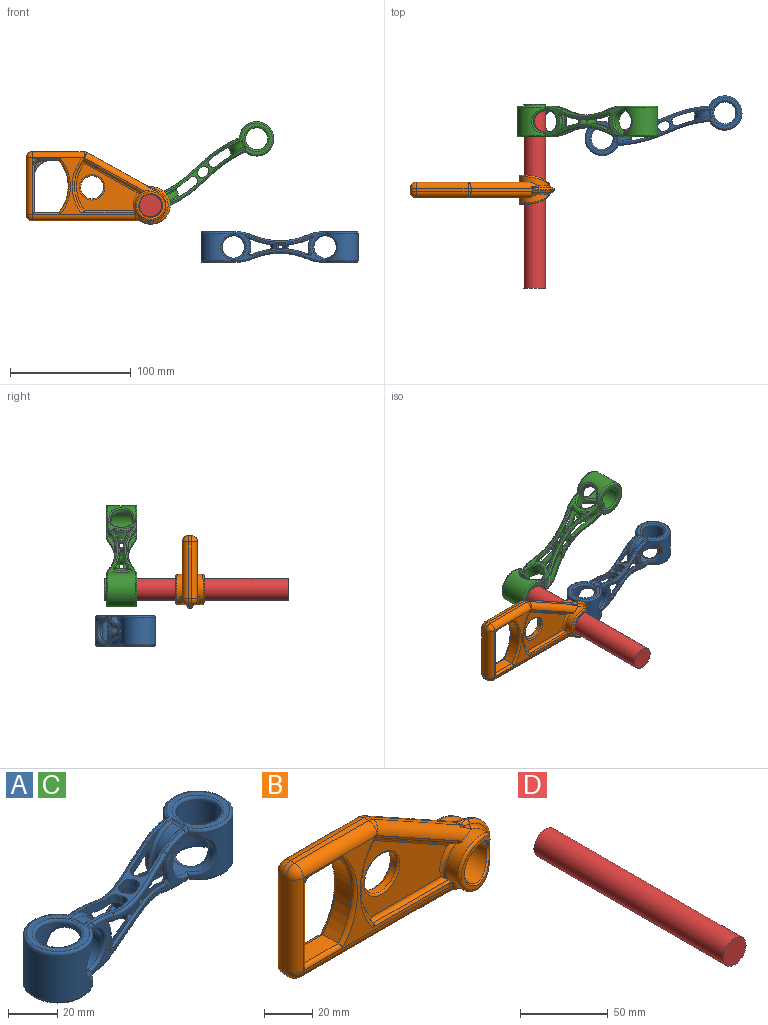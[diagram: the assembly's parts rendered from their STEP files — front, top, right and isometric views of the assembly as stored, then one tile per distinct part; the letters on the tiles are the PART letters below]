
ASSEMBLY  parts=4 mates=2
PART A: 148 faces, bbox 132.7x52.1x26.6 mm
  f0: extruded ~21.29x15.47mm, area 60mm2, adj f2,f5,f6,f9,f89,f90,f106,f124
  f1: extruded ~30.64x19.59mm, area 94.2mm2, adj f2,f3,f4,f11,f13,f15,f17,f19
  f2: bspline ~51.5x17.79mm, area 103.2mm2, adj f0,f1,f8,f109,f111,f130,f131,f132
  f3: extruded ~25.18x24.71mm, area 181.7mm2, adj f1,f34,f55,f56,f59,f64,f94,f95
  f4: extruded ~25.24x22.45mm, area 174.2mm2, adj f1,f35,f55,f56,f60,f63,f96,f98
  f5: extruded ~25.36x23.65mm, area 171.9mm2, adj f0,f38,f55,f56,f58,f61,f89,f91
  f6: extruded ~25.85x25.34mm, area 182.8mm2, adj f0,f39,f55,f56,f57,f62,f90,f92
  f7: extruded ~76.15x22.86mm, area 322.9mm2, adj f26,f27,f45,f47,f65,f67,f69,f71
  f8: extruded ~76.19x22.86mm, area 349.2mm2, adj f2,f26,f27,f43,f48,f68,f70,f72
  f9: cylinder r=7.62mm len=3.81mm, axis (0,0,-1), area 1.8mm2, adj f0,f56,f124,f126
  f10: cylinder r=7.62mm len=3.81mm, axis (0,0,-1), area 1.8mm2, adj f55,f99,f112,f113
  f11: cylinder r=7.62mm len=3.91mm, axis (0,0,-1), area 1.9mm2, adj f1,f56,f114,f115
  f12: cylinder r=7.62mm len=3.91mm, axis (0,0,-1), area 1.9mm2, adj f55,f99,f121,f123
  f13: cylinder r=5.08mm len=3.89mm, axis (0,0,-1), area 8.8mm2, adj f1,f56,f120,f122
  f14: cylinder r=5.08mm len=3.89mm, axis (0,0,-1), area 8.8mm2, adj f55,f99,f116,f118
  f15: cylinder r=5.08mm len=3.88mm, axis (0,0,-1), area 8.6mm2, adj f1,f56,f125,f127
  f16: cylinder r=5.08mm len=3.88mm, axis (0,0,-1), area 8.6mm2, adj f55,f99,f117,f119
  f17: extruded ~3.88x2.73mm, area 11.3mm2, adj f1,f56,f122,f125
  f18: extruded ~3.88x2.73mm, area 11.3mm2, adj f55,f99,f116,f117
  f19: extruded ~3.88x2.98mm, area 12.2mm2, adj f1,f56,f120,f127
  f20: extruded ~3.88x2.98mm, area 12.2mm2, adj f55,f99,f118,f119
  f21: plane 27.31x26.12mm, normal (0,0,1), area 177.8mm2, adj f33,f34,f35,f53,f59,f60,f85,f87
  f22: plane 27.87x26.19mm, normal (0,0,1), area 179.1mm2, adj f38,f39,f40,f54,f57,f58,f77,f78
  f23: plane 27.31x26.12mm, normal (0,0,-1), area 177.8mm2, adj f34,f35,f36,f51,f63,f64,f73,f75
  f24: plane 27.87x26.19mm, normal (0,0,-1), area 179.1mm2, adj f37,f38,f39,f52,f61,f62,f65,f66
  f25: cylinder r=9.14mm len=22.73mm, axis (0,0,-1), area 886.6mm2, adj f41,f51,f53
  f26: cylinder r=14.22mm len=28.45mm, axis (0,0,-1), area 1302.5mm2, adj f7,f8,f42,f43,f44,f45,f75,f87
  f27: cylinder r=14.22mm len=28.45mm, axis (0,0,-1), area 1277mm2, adj f7,f8,f46,f47,f48,f49,f66,f78
  f28: cylinder r=9.14mm len=22.73mm, axis (0,0,-1), area 864.6mm2, adj f50,f52,f54
  f29: cylinder r=9.27mm len=25.51mm, axis (0,1,0), area 486.9mm2, adj f46,f47,f48,f49,f50
  f30: cylinder r=9.27mm len=25.34mm, axis (0,1,0), area 493.1mm2, adj f41,f42,f43,f44,f45
  f31: cylinder r=11.81mm len=23.62mm, axis (0,1,0), area 180.4mm2, adj f37,f38,f39,f40
  f32: cylinder r=11.81mm len=23.62mm, axis (0,1,0), area 184.8mm2, adj f33,f34,f35,f36
  f33: bspline ~8.37x2.03mm, area 10.5mm2, adj f21,f32,f34,f35
  f34: bspline ~26.3x16.67mm, area 89mm2, adj f3,f21,f23,f32,f33,f36,f59,f64
  f35: bspline ~26.3x16.17mm, area 77.2mm2, adj f4,f21,f23,f32,f33,f36,f60,f63
  f36: bspline ~8.37x2.03mm, area 10.5mm2, adj f23,f32,f34,f35
  f37: bspline ~8.33x1.96mm, area 10.2mm2, adj f24,f31,f38,f39
  f38: bspline ~26.3x15.72mm, area 76.6mm2, adj f5,f22,f24,f31,f37,f40,f58,f61
  f39: bspline ~26.3x16.12mm, area 86.8mm2, adj f6,f22,f24,f31,f37,f40,f57,f62
  f40: bspline ~8.33x1.96mm, area 10.2mm2, adj f22,f31,f38,f39
  f41: bspline ~20.62x20.42mm, area 176.2mm2, adj f25,f30
  f42: bspline ~21.13x10.93mm, area 61mm2, adj f26,f30,f43
  f43: bspline ~21.24x13.49mm, area 62.6mm2, adj f8,f26,f30,f42
  f44: bspline ~21.18x11.16mm, area 65.1mm2, adj f26,f30,f45
  f45: bspline ~21.22x12.66mm, area 70.2mm2, adj f7,f26,f30,f44
  f46: bspline ~21.2x11.48mm, area 64.5mm2, adj f27,f29,f47
  f47: bspline ~21.22x12.32mm, area 61.2mm2, adj f7,f27,f29,f46
  f48: bspline ~21.23x13.02mm, area 67.6mm2, adj f8,f27,f29,f49
  f49: bspline ~21.21x11.56mm, area 68.4mm2, adj f27,f29,f48
  f50: bspline ~20.83x20.62mm, area 177.5mm2, adj f28,f29
  f51: torus R=10.48mm, axis (0,0,1), area 126.8mm2, adj f23,f25
  f52: torus R=10.48mm, axis (0,0,1), area 126.8mm2, adj f24,f28
  f53: torus R=10.48mm, axis (0,0,1), area 126.8mm2, adj f21,f25
  f54: torus R=10.48mm, axis (0,0,1), area 126.8mm2, adj f22,f28
  f55: cylinder r=57.15mm len=45.21mm, axis (0,1,0), area 182.1mm2, adj f3,f4,f5,f6,f10,f12,f14,f16
  f56: cylinder r=57.15mm len=45.21mm, axis (0,1,0), area 182.1mm2, adj f3,f4,f5,f6,f9,f11,f13,f15
  f57: cylinder r=34.92mm len=13.81mm, axis (0,1,0), area 18.5mm2, adj f6,f22,f39,f56,f82
  f58: cylinder r=34.92mm len=13.81mm, axis (0,1,0), area 17.9mm2, adj f5,f22,f38,f56,f79
  f59: cylinder r=34.92mm len=13.81mm, axis (0,1,0), area 18.2mm2, adj f3,f21,f34,f56,f83
  f60: cylinder r=34.92mm len=13.81mm, axis (0,1,0), area 18.5mm2, adj f4,f21,f35,f56,f86
  f61: cylinder r=34.92mm len=13.81mm, axis (0,1,0), area 17.9mm2, adj f5,f24,f38,f55,f67
  f62: cylinder r=34.92mm len=13.81mm, axis (0,1,0), area 18.5mm2, adj f6,f24,f39,f55,f70
  f63: cylinder r=34.92mm len=13.81mm, axis (0,1,0), area 18.5mm2, adj f4,f23,f35,f55,f74
  f64: cylinder r=34.92mm len=13.81mm, axis (0,1,0), area 18.2mm2, adj f3,f23,f34,f55,f71
  f65: bspline ~12.89x2.51mm, area 4.9mm2, adj f7,f24,f66,f67
  f66: torus R=12.95mm, axis (0,0,1), area 148.7mm2, adj f24,f27,f65,f68
  f67: bspline ~21.36x5.74mm, area 28.7mm2, adj f7,f61,f65,f69
  f68: bspline ~14.57x2.58mm, area 4.4mm2, adj f8,f24,f66,f70
  f69: bspline ~57.28x19.04mm, area 98.7mm2, adj f7,f55,f67,f71
  f70: bspline ~21.47x5.74mm, area 27.8mm2, adj f8,f62,f68,f72
  f71: bspline ~21.5x5.74mm, area 27.8mm2, adj f7,f64,f69,f73
  f72: bspline ~57.29x19.01mm, area 99.1mm2, adj f8,f55,f70,f74
  f73: bspline ~13.03x2.5mm, area 3.3mm2, adj f7,f23,f71,f75
  f74: bspline ~21.37x5.75mm, area 28.8mm2, adj f8,f63,f72,f76
  f75: torus R=12.95mm, axis (0,0,1), area 148.7mm2, adj f23,f26,f73,f76
  f76: bspline ~8.98x1.98mm, area 4mm2, adj f8,f23,f74,f75
  f77: bspline ~12.89x2.51mm, area 4.9mm2, adj f7,f22,f78,f79
  f78: torus R=12.95mm, axis (0,0,1), area 148.7mm2, adj f22,f27,f77,f80
  f79: bspline ~18.69x4.4mm, area 28.7mm2, adj f7,f58,f77,f81
  f80: bspline ~14.57x2.58mm, area 4.4mm2, adj f8,f22,f78,f82
  f81: bspline ~57.28x19.04mm, area 98.7mm2, adj f7,f56,f79,f83
  f82: bspline ~18.81x4.4mm, area 27.8mm2, adj f8,f57,f80,f84
  f83: bspline ~21.5x5.74mm, area 27.8mm2, adj f7,f59,f81,f85
  f84: bspline ~57.29x19.01mm, area 99.1mm2, adj f8,f56,f82,f86
  f85: bspline ~8.13x1.88mm, area 3.3mm2, adj f7,f21,f83,f87
  f86: bspline ~21.37x5.75mm, area 28.8mm2, adj f8,f60,f84,f88
  f87: torus R=12.95mm, axis (0,0,1), area 148.7mm2, adj f21,f26,f85,f88
  f88: bspline ~14.31x2.75mm, area 4mm2, adj f8,f21,f86,f87
  f89: extruded ~2.04x1.8mm, area 3mm2, adj f0,f5,f91,f102,f104
  f90: extruded ~1.99x1.59mm, area 2.6mm2, adj f0,f6,f92,f109
  f91: extruded ~14.24x1.9mm, area 16.2mm2, adj f5,f89,f93,f102
  f92: extruded ~12.09x1.92mm, area 18.9mm2, adj f6,f90,f108,f109,f142
  f93: extruded ~2.04x1.8mm, area 3mm2, adj f5,f91,f99,f100,f102
  f94: extruded ~1.32x0.58mm, area 0.8mm2, adj f3,f95,f99,f103
  f95: extruded ~13.32x1.86mm, area 21.3mm2, adj f3,f94,f97,f103,f105,f107
  f96: extruded ~11.05x1.58mm, area 11.8mm2, adj f4,f98,f110,f146
  f97: extruded ~1.32x0.58mm, area 0.8mm2, adj f1,f3,f95,f107
  f98: extruded ~1.55x0.65mm, area 0.9mm2, adj f1,f4,f96,f110,f111
  f99: extruded ~48.28x26.48mm, area 295mm2, adj f3,f4,f5,f6,f10,f12,f14,f16
  f100: bspline ~9.02x4.12mm, area 7.9mm2, adj f7,f93,f101,f102
  f101: bspline ~48.33x17.11mm, area 103.5mm2, adj f7,f99,f100,f103,f129
  f102: bspline ~21.94x6.22mm, area 37.4mm2, adj f7,f89,f91,f93,f100,f104
  f103: bspline ~7.71x3.89mm, area 4.2mm2, adj f7,f94,f95,f101,f105
  f104: bspline ~9.03x4.12mm, area 7.9mm2, adj f7,f89,f102,f106
  f105: bspline ~21.06x5.32mm, area 30.4mm2, adj f7,f95,f103,f107
  f106: bspline ~52.48x18.04mm, area 103.5mm2, adj f0,f1,f7,f104,f107,f129,f136
  f107: bspline ~7.71x3.89mm, area 4.2mm2, adj f7,f95,f97,f105,f106
  f108: bspline ~19.16x5.8mm, area 27mm2, adj f8,f92,f109,f140
  f109: bspline ~7.9x3.57mm, area 7.4mm2, adj f2,f8,f90,f92,f108
  f110: bspline ~18.57x5.5mm, area 29.5mm2, adj f8,f96,f98,f111,f147
  f111: bspline ~5.82x3.12mm, area 4mm2, adj f2,f8,f98,f110
  f112: cylinder r=3.46mm len=4.71mm, axis (0,0,-1), area 21.9mm2, adj f6,f10,f55,f99
  f113: cylinder r=3.46mm len=4.51mm, axis (0,0,-1), area 20.2mm2, adj f5,f10,f55,f99
  f114: cylinder r=3.46mm len=4.53mm, axis (0,0,-1), area 21.5mm2, adj f1,f3,f11,f56
  f115: cylinder r=3.46mm len=4.64mm, axis (0,0,-1), area 21.9mm2, adj f1,f4,f11,f56
  f116: cylinder r=3.46mm len=3.98mm, axis (0,0,-1), area 15mm2, adj f14,f18,f55,f99
  f117: cylinder r=3.46mm len=3.92mm, axis (0,0,-1), area 14.8mm2, adj f16,f18,f55,f99
  f118: cylinder r=3.46mm len=4.52mm, axis (0,0,-1), area 20.8mm2, adj f14,f20,f55,f99
  f119: cylinder r=3.46mm len=4.51mm, axis (0,0,-1), area 20.6mm2, adj f16,f20,f55,f99
  f120: cylinder r=3.46mm len=4.52mm, axis (0,0,-1), area 20.8mm2, adj f1,f13,f19,f56
  f121: cylinder r=3.46mm len=4.53mm, axis (0,0,-1), area 21.5mm2, adj f3,f12,f55,f99
  f122: cylinder r=3.46mm len=3.98mm, axis (0,0,-1), area 15mm2, adj f1,f13,f17,f56
  f123: cylinder r=3.46mm len=4.64mm, axis (0,0,-1), area 21.9mm2, adj f4,f12,f55,f99
  f124: cylinder r=3.46mm len=4.51mm, axis (0,0,-1), area 20.2mm2, adj f0,f5,f9,f56
  f125: cylinder r=3.46mm len=3.92mm, axis (0,0,-1), area 14.8mm2, adj f1,f15,f17,f56
  f126: cylinder r=3.46mm len=4.71mm, axis (0,0,-1), area 21.9mm2, adj f0,f6,f9,f56
  f127: cylinder r=3.46mm len=4.51mm, axis (0,0,-1), area 20.6mm2, adj f1,f15,f19,f56
  f128: plane 3.49x0.98mm, normal (0.73,0.68,0), area 4.5mm2, adj f1,f99,f129,f133
  f129: extruded ~3.66x0.73mm, area 2.8mm2, adj f101,f106,f128,f130
  f130: cylinder r=7.24mm len=9.26mm, axis (0,0,-1), area 39.7mm2, adj f0,f2,f99,f129,f131
  f131: extruded ~2.91x1.03mm, area 3.2mm2, adj f2,f99,f130,f132
  f132: plane 2.84x1.17mm, normal (0.99,0.11,0), area 3.3mm2, adj f1,f2,f99,f131,f133
  f133: cylinder r=5.46mm len=6.98mm, axis (0,0,-1), area 27.1mm2, adj f1,f99,f128,f132
  f134: extruded ~3.34x1.12mm, area 3.9mm2, adj f1,f99,f135,f139
  f135: cylinder r=7.24mm len=9.56mm, axis (0,0,-1), area 34.8mm2, adj f1,f99,f134,f136
  f136: extruded ~2.88x0.84mm, area 2.6mm2, adj f99,f106,f135,f137
  f137: plane 2.82x1.24mm, normal (-1,-0.01,0), area 3.5mm2, adj f1,f99,f136,f138
  f138: cylinder r=5.46mm len=7.61mm, axis (0,0,-1), area 26.1mm2, adj f1,f99,f137,f139
  f139: plane 3.15x0.85mm, normal (-0.78,-0.63,0), area 3.4mm2, adj f1,f99,f134,f138
  f140: bspline ~3.6x2.85mm, area 1.7mm2, adj f108,f141,f142
  f141: bspline ~2.71x1.44mm, area 1.3mm2, adj f8,f140,f143
  f142: cylinder r=1mm len=1.76mm, axis (0,1,0), area 3.7mm2, adj f6,f92,f99,f140,f143
  f143: bspline ~2.21x1.41mm, area 1.6mm2, adj f8,f141,f142,f144
  f144: bspline ~49.46x17.16mm, area 78.5mm2, adj f8,f99,f143,f145
  f145: bspline ~3.74x1.12mm, area 2.5mm2, adj f8,f144,f147
  f146: cylinder r=1mm len=1.37mm, axis (0,1,0), area 2mm2, adj f4,f96,f99,f147
  f147: bspline ~4.04x2.93mm, area 4.1mm2, adj f99,f110,f145,f146
PART B: 126 faces, bbox 120.1x24.8x62.2 mm
  f0: cylinder r=12.7mm len=25.4mm, axis (0,1,0), area 303mm2, adj f3,f5,f13,f14,f29,f34,f51,f52
  f1: plane 50.55x28.14mm, normal (0.49,0,0.87), area 146.9mm2, adj f4,f5,f55,f99
  f2: plane 88.75x3.47mm, normal (0,0,-1), area 226.3mm2, adj f6,f7,f62,f66,f68,f106
  f3: plane 5.08x4.35mm, normal (0,0,-1), area 10.5mm2, adj f0,f7,f107
  f4: cylinder r=5.08mm len=58.16mm, axis (0.87,0,-0.49), area 477.1mm2, adj f1,f18,f28,f54,f96,f97,f98
  f5: cylinder r=5.08mm len=58.16mm, axis (-0.87,0,0.49), area 477.1mm2, adj f0,f1,f29,f57,f101,f103,f105
  f6: bspline ~14.3x6.92mm, area 49.7mm2, adj f2,f27,f53,f62,f102,f104
  f7: bspline ~14.3x6.92mm, area 49.7mm2, adj f2,f3,f52,f68,f108,f109
  f8: bspline ~4.65x4.65mm, area 4.9mm2, adj f41,f43,f85
  f9: bspline ~4.65x4.65mm, area 5mm2, adj f45,f47,f82
  f10: plane 5.39x5.15mm, normal (0,-1,0), area 8.3mm2, adj f72,f75,f76,f87
  f11: plane 5.38x5.15mm, normal (0,1,0), area 8.3mm2, adj f73,f77,f78,f84
  f12: plane 85.72x47mm, normal (0,-1,0), area 413.2mm2, adj f16,f41,f42,f43,f44,f50,f53,f56
  f13: plane 44.79x6.22mm, normal (0,0,1), area 167.5mm2, adj f0,f15,f29,f33,f34,f36,f52
  f14: plane 48.43x26.96mm, normal (-0.49,0,-0.87), area 7.2mm2, adj f0,f15,f35,f51
  f15: extruded ~44.64x8.78mm, area 92.7mm2, adj f13,f14,f29,f36,f51
  f16: plane 46.83x4.1mm, normal (0,0,1), area 88.9mm2, adj f12,f18,f30,f40,f50,f53
  f17: plane 15.24x9.02mm, normal (0,0,-1), area 112.1mm2, adj f31,f41,f45,f76,f77,f79,f80,f81
  f18: cylinder r=12.7mm len=25.4mm, axis (0,1,0), area 303mm2, adj f4,f16,f24,f27,f28,f38,f49,f53
  f19: cylinder r=9.14mm len=22.93mm, axis (0,1,0), area 1317.4mm2, adj f90,f91
  f20: extruded ~23.87x22.99mm, area 136.8mm2, adj f89,f90
  f21: extruded ~23.87x22.99mm, area 136.8mm2, adj f88,f91
  f22: plane 20.32x9.02mm, normal (0,0,1), area 183.3mm2, adj f23,f31,f44,f48
  f23: plane 38.1x9.02mm, normal (1,0,0), area 321.8mm2, adj f22,f43,f47,f70,f71,f72,f73,f74
  f24: plane 48.43x26.96mm, normal (-0.49,0,-0.87), area 7.2mm2, adj f18,f30,f37,f49
  f25: plane 43.04x2.54mm, normal (0,0,1), area 109.3mm2, adj f55,f56,f59,f60
  f26: plane 46.99x2.54mm, normal (-1,0,0), area 119.4mm2, adj f60,f61,f65,f66
  f27: plane 5.08x4.35mm, normal (0,0,-1), area 10.5mm2, adj f6,f18,f100
  f28: plane 50.03x27.8mm, normal (0,-1,0), area 3.7mm2, adj f4,f18,f49,f56
  f29: plane 92.93x47.88mm, normal (0,1,0), area 506.6mm2, adj f0,f5,f13,f15,f45,f46,f47,f48
  f30: extruded ~43.18x7.62mm, area 6.1mm2, adj f16,f24,f39,f50
  f31: extruded ~43.18x9.02mm, area 421mm2, adj f17,f22,f42,f46
  f32: plane 50.98x38.97mm, normal (0,-1,0), area 959.1mm2, adj f37,f38,f39,f40,f94
  f33: plane 50.98x40.81mm, normal (0,1,0), area 1033.1mm2, adj f13,f34,f35,f36,f93
  f34: torus R=14.54mm, axis (0,-1,0), area 50.5mm2, adj f0,f13,f33,f35
  f35: cylinder r=1.84mm len=49.32mm, axis (-0.87,0,0.49), area 154mm2, adj f14,f33,f34,f36
  f36: bspline ~45.12x10.4mm, area 132.1mm2, adj f13,f15,f33,f35
  f37: cylinder r=1.84mm len=49.32mm, axis (0.87,0,-0.49), area 154mm2, adj f24,f32,f38,f39
  f38: torus R=14.54mm, axis (0,-1,0), area 47.9mm2, adj f18,f32,f37,f40
  f39: bspline ~44.05x9.54mm, area 128.7mm2, adj f30,f32,f37,f40
  f40: cylinder r=1.84mm len=44.22mm, axis (-1,0,0), area 122.6mm2, adj f16,f32,f38,f39
  f41: cylinder r=1.84mm len=23.04mm, axis (-1,0,0), area 53.4mm2, adj f8,f12,f17,f42,f85
  f42: bspline ~47.98x10.47mm, area 140mm2, adj f12,f31,f41,f44
  f43: cylinder r=1.84mm len=46.86mm, axis (0,0,-1), area 120.9mm2, adj f8,f12,f23,f44,f85
  f44: cylinder r=1.84mm len=23.04mm, axis (1,0,0), area 62.7mm2, adj f12,f22,f42,f43
  f45: cylinder r=1.84mm len=23.04mm, axis (1,0,0), area 53.4mm2, adj f9,f17,f29,f46,f82
  f46: bspline ~47.98x10.47mm, area 140mm2, adj f29,f31,f45,f48
  f47: cylinder r=1.84mm len=46.86mm, axis (0,0,1), area 120.9mm2, adj f9,f23,f29,f48,f82
  f48: cylinder r=1.84mm len=23.04mm, axis (-1,0,0), area 62.7mm2, adj f22,f29,f46,f47
  f49: cylinder r=1.84mm len=51.56mm, axis (-0.87,0,0.49), area 163.9mm2, adj f18,f24,f28,f50,f56
  f50: bspline ~48.07x11mm, area 137.5mm2, adj f12,f16,f30,f49,f56
  f51: cylinder r=1.84mm len=50.31mm, axis (0.87,0,-0.49), area 161.4mm2, adj f0,f14,f15,f29
  f52: torus R=14.54mm, axis (0,-1,0), area 20mm2, adj f0,f7,f13,f29
  f53: torus R=14.54mm, axis (0,-1,0), area 20mm2, adj f6,f12,f16,f18
  f54: sphere r=5.08mm, area 13.1mm2, adj f4,f55,f56
  f55: cylinder r=5.08mm len=2.54mm, axis (0,1,0), area 6.6mm2, adj f1,f25,f54,f57
  f56: cylinder r=5.08mm len=43.04mm, axis (1,0,0), area 343.3mm2, adj f12,f25,f28,f49,f50,f54,f58
  f57: sphere r=5.08mm, area 13.1mm2, adj f5,f55,f59
  f58: sphere r=5.08mm, area 40.5mm2, adj f56,f60,f61
  f59: cylinder r=5.08mm len=43.04mm, axis (-1,0,0), area 343.4mm2, adj f25,f29,f57,f63
  f60: cylinder r=5.08mm len=5.08mm, axis (0,1,0), area 20.3mm2, adj f25,f26,f58,f63
  f61: cylinder r=5.08mm len=46.99mm, axis (0,0,1), area 375mm2, adj f12,f26,f58,f64
  f62: cylinder r=5.08mm len=85.72mm, axis (-1,0,0), area 684mm2, adj f2,f6,f12,f64
  f63: sphere r=5.08mm, area 55.3mm2, adj f59,f60,f65
  f64: sphere r=5.08mm, area 40.5mm2, adj f61,f62,f66
  f65: cylinder r=5.08mm len=46.99mm, axis (0,0,-1), area 375mm2, adj f26,f29,f63,f67
  f66: cylinder r=5.08mm len=5.08mm, axis (0,1,0), area 20.3mm2, adj f2,f26,f64,f67
  f67: sphere r=5.08mm, area 40.5mm2, adj f65,f66,f68
  f68: cylinder r=5.08mm len=85.72mm, axis (1,0,0), area 684mm2, adj f2,f7,f29,f67
  f69: extruded ~11.34x10.3mm, area 6.3mm2, adj f70,f75,f78,f81
  f70: cylinder r=1.07mm len=0.41mm, axis (0,1,0), area 0.2mm2, adj f23,f69,f71,f74
  f71: bspline ~4.79x2.21mm, area 5.1mm2, adj f23,f70,f72,f75
  f72: cylinder r=1.07mm len=1.11mm, axis (0,0,1), area 1.9mm2, adj f10,f23,f71,f87
  f73: cylinder r=1.07mm len=1.11mm, axis (0,0,-1), area 1.9mm2, adj f11,f23,f74,f84
  f74: bspline ~4.9x2.29mm, area 5.1mm2, adj f23,f70,f73,f78
  f75: bspline ~13.88x13.62mm, area 19.6mm2, adj f10,f69,f71,f79
  f76: cylinder r=1.07mm len=1.35mm, axis (1,0,0), area 2.3mm2, adj f10,f17,f79,f87
  f77: cylinder r=1.07mm len=1.35mm, axis (-1,0,0), area 2.3mm2, adj f11,f17,f80,f84
  f78: bspline ~13.69x13.14mm, area 19.6mm2, adj f11,f69,f74,f80
  f79: bspline ~5.68x2.23mm, area 5.7mm2, adj f17,f75,f76,f81
  f80: bspline ~5.89x2.3mm, area 5.6mm2, adj f17,f77,f78,f81
  f81: cylinder r=1.07mm len=0.39mm, axis (0,1,0), area 0.1mm2, adj f17,f69,f79,f80
  f82: bspline ~5.84x5.84mm, area 12.8mm2, adj f9,f45,f47,f83
  f83: cylinder r=5.08mm len=5.08mm, axis (0,-1,0), area 17.3mm2, adj f17,f23,f82,f84
  f84: torus R=4.01mm, axis (0,-1,0), area 12.4mm2, adj f11,f73,f77,f83
  f85: bspline ~5.84x5.84mm, area 12.8mm2, adj f8,f41,f43,f86
  f86: cylinder r=5.08mm len=5.08mm, axis (0,-1,0), area 17.3mm2, adj f17,f23,f85,f87
  f87: torus R=4.01mm, axis (0,-1,0), area 12.4mm2, adj f10,f72,f76,f86
  f88: bspline ~25.43x25.42mm, area 132.1mm2, adj f0,f21
  f89: bspline ~25.43x25.41mm, area 132.1mm2, adj f18,f20
  f90: bspline ~19.97x19.59mm, area 60.3mm2, adj f19,f20
  f91: bspline ~19.97x19.59mm, area 60mm2, adj f19,f21
  f92: cylinder r=9.49mm len=18.97mm, axis (0,-1,0), area 183.6mm2, adj f93,f94
  f93: torus R=10.49mm, axis (0,-1,0), area 97.2mm2, adj f33,f92
  f94: torus R=10.49mm, axis (0,-1,0), area 97.2mm2, adj f32,f92
  f95: extruded ~30.96x24.73mm, area 43.6mm2, adj f99,f106,f112,f113,f114,f115,f120,f121
  f96: cylinder r=1.84mm len=6.39mm, axis (0.87,0,-0.49), area 6mm2, adj f4,f98,f110,f111,f112
  f97: bspline ~3.98x2.1mm, area 1.2mm2, adj f4,f99,f110
  f98: torus R=14.54mm, axis (0,-1,0), area 103.8mm2, adj f4,f18,f96,f100,f113
  f99: cylinder r=1.84mm len=2.54mm, axis (0,1,0), area 2.7mm2, adj f1,f95,f97,f101,f111,f119
  f100: cylinder r=1.84mm len=5.08mm, axis (1,0,0), area 11mm2, adj f27,f98,f102,f114
  f101: bspline ~3.98x2.1mm, area 1.2mm2, adj f5,f99,f118
  f102: bspline ~6.76x2.16mm, area 4.2mm2, adj f6,f100,f115,f116,f117
  f103: cylinder r=1.84mm len=6.39mm, axis (-0.87,0,0.49), area 6mm2, adj f5,f105,f118,f119,f120
  f104: bspline ~3x1.46mm, area 0.9mm2, adj f6,f106,f116
  f105: torus R=14.54mm, axis (0,-1,0), area 104.2mm2, adj f0,f5,f103,f107,f121
  f106: cylinder r=1.84mm len=3.45mm, axis (0,1,0), area 3.6mm2, adj f2,f95,f104,f108,f117,f124
  f107: cylinder r=1.84mm len=5.08mm, axis (-1,0,0), area 11mm2, adj f3,f105,f109,f122
  f108: bspline ~3x1.46mm, area 0.9mm2, adj f7,f106,f125
  f109: bspline ~6.76x2.16mm, area 4.2mm2, adj f7,f107,f123,f124,f125
  f110: bspline ~3.12x2.25mm, area 1.3mm2, adj f96,f97,f111
  f111: bspline ~1.44x0.99mm, area 0.1mm2, adj f96,f99,f110,f112
  f112: bspline ~6.1x2.56mm, area 9.1mm2, adj f95,f96,f111,f113
  f113: bspline ~30.93x18.26mm, area 120.5mm2, adj f95,f98,f112,f114
  f114: bspline ~6.93x2.01mm, area 12.6mm2, adj f95,f100,f113,f115
  f115: bspline ~4.39x2.4mm, area 4.7mm2, adj f95,f102,f114,f117
  f116: bspline ~2.39x1.73mm, area 0.9mm2, adj f102,f104,f117
  f117: bspline ~1.22x1.06mm, area 0.1mm2, adj f102,f106,f115,f116
  f118: bspline ~2.83x2.09mm, area 1.3mm2, adj f101,f103,f119
  f119: bspline ~1.44x0.99mm, area 0.1mm2, adj f99,f103,f118,f120
  f120: bspline ~6.1x2.56mm, area 9.1mm2, adj f95,f103,f119,f121
  f121: bspline ~30.93x18.26mm, area 120.5mm2, adj f95,f105,f120,f122
  f122: bspline ~6.93x2.01mm, area 12.6mm2, adj f95,f107,f121,f123
  f123: bspline ~4.39x2.4mm, area 4.7mm2, adj f95,f109,f122,f124
  f124: bspline ~1.22x1.06mm, area 0.1mm2, adj f106,f109,f123,f125
  f125: bspline ~2.36x1.71mm, area 0.9mm2, adj f108,f109,f124
PART C: same geometry as A
PART D: 3 faces, bbox 18.3x152.4x18.3 mm
  f0: cylinder r=9.14mm len=152.4mm, axis (0,1,0), area 8755.9mm2, adj f1,f2
  f1: plane 18.29x18.29mm, normal (0,-1,0), area 262.7mm2, adj f0
  f2: plane 18.29x18.29mm, normal (0,1,0), area 262.7mm2, adj f0
PLACE A t=(154.75,56.68,-61.65)mm
PLACE B t=(-9.94,-13.42,-6.01)mm fixed
PLACE C rot(axis=(0.13,0.7,-0.7),165.6deg) t=(69.37,43.23,-20.57)mm
PLACE D t=(93.11,-18.66,-61.59)mm
MATE slider D.f0 <-> B.f0  axis (0,1,0) through (33.26,-18.66,-27.24)mm
MATE cylindrical C.f25 <-> D.f0  axis (0,1,0) through (33.26,43.23,-27.24)mm
